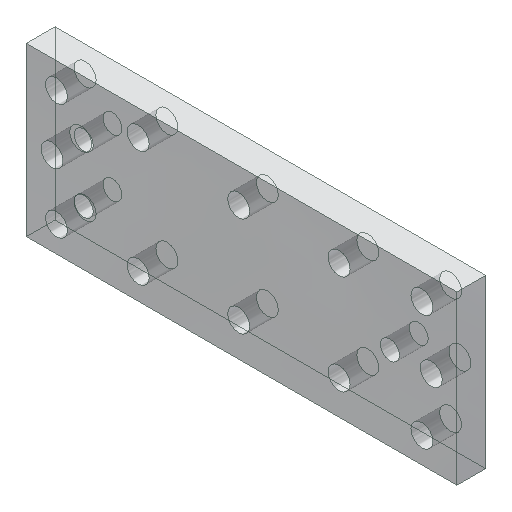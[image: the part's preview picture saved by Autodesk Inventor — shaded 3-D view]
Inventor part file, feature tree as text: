
AUTODESK INVENTOR PART (.ipt)
format: ipt  version: 2025 (Build 290162000, 162)  size: 157,184 bytes
history: native  units: mm
features: other x1, extrude x1, sketch x1
ambient origin geometry x8: Origin, YZ Plane, XZ Plane, XY Plane, X Axis, Y Axis, Z Axis, Center Point
bodies: Body1 (feature_tree)
feature tree (3):
  other  "Sólido1"
  extrude  "Extrusão1"  [1 undecoded]
  sketch  "Esboço1"  dims[d0=6.0mm d1=0.0mm]
note: 1 required parameter value undecoded (feature->parameter linkage not recoverable at this tier; creation-order binding heuristic only, values carry confidence <= 0.55)
